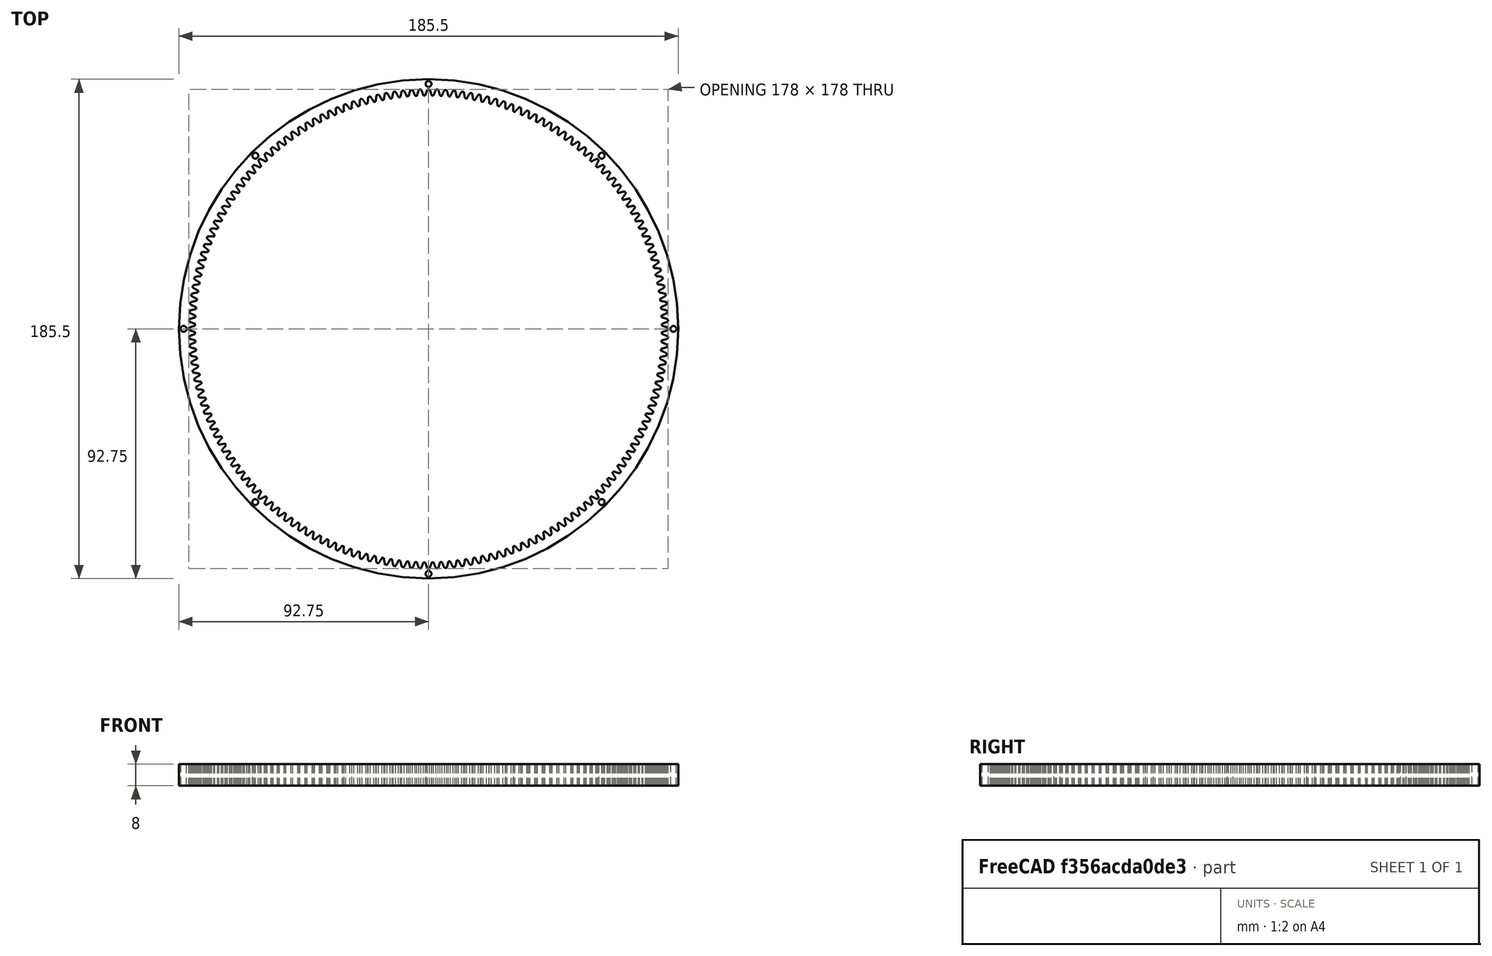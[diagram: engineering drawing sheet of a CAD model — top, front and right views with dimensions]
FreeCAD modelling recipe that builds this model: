
FCSTD DOCUMENT  (FreeCAD 0.19R24276 (Git))
Label: Out_gear_t176_d185_5_otv
License: All rights reserved
LicenseURL: http://en.wikipedia.org/wiki/All_rights_reserved
objects: Part::FeaturePython×1, Part::Cylinder×1, Part::Cut×1, Sketcher::SketchObject×1, PartDesign::FeatureBase×1, PartDesign::Pocket×1, PartDesign::Body×1
note: 8 computed .brp shape members not serialized (recipe doc carries the construction recipe); baked Part::Feature solids carry a one-line shape summary decoded from their .brp

FEATURE [Part::FeaturePython] involutegear  # WARN: FeaturePython — macro-defined, semantics opaque (R4)
  AttacherType = Attacher::AttachEngine3D
  backlash = 0
  beta = 0
  clearance = 0.25
  da = 178
  df = 173.5
  double_helix = false
  dw = 176
  head = 0
  height = 8
  module = 1
  numpoints = 6
  pressure_angle = 20
  properties_from_tool = false
  reversed_backlash = false
  shift = 0
  simple = false
  teeth = 176
  transverse_pitch = 3.14159
  undercut = false
  version = 0.0.3
FEATURE [Part::Cylinder] Cylinder  label="Цилиндр"
  Angle = 360
  AttacherType = Attacher::AttachEngine3D
  Height = 8
  Radius = 92.75
FEATURE [Part::Cut] Cut
  Base = -> Cylinder
  Tool = -> involutegear
FEATURE [Sketcher::SketchObject] Sketch
  FullyConstrained = false
  MapMode = 5
  Support = -> [XY_Plane]
  sketch-geometry (17):
    g0: LineSegment StartX=0 StartY=0 StartZ=0 EndX=64.3467 EndY=64.3467 EndZ=0
    g1: Circle CenterX=0 CenterY=0 CenterZ=0 NormalX=0 NormalY=0 NormalZ=1 AngleXU=0 Radius=91
    g2: Circle CenterX=64.3467 CenterY=64.3467 CenterZ=0 NormalX=0 NormalY=0 NormalZ=1 AngleXU=0 Radius=1.1
    g3: LineSegment StartX=0 StartY=0 StartZ=0 EndX=-1.5e-15 EndY=91 EndZ=0
    g4: LineSegment StartX=0 StartY=0 StartZ=0 EndX=91 EndY=0 EndZ=0
    g5: Circle CenterX=-1.5e-15 CenterY=91 CenterZ=0 NormalX=0 NormalY=0 NormalZ=1 AngleXU=0 Radius=1.1
    g6: Circle CenterX=91 CenterY=0 CenterZ=0 NormalX=0 NormalY=0 NormalZ=1 AngleXU=0 Radius=1.1
    g7: Circle CenterX=64.3467 CenterY=-64.3467 CenterZ=0 NormalX=0 NormalY=0 NormalZ=1 AngleXU=0 Radius=1.1
    g8: Circle CenterX=-1.5e-15 CenterY=-91 CenterZ=0 NormalX=0 NormalY=0 NormalZ=1 AngleXU=0 Radius=1.1
    g9: LineSegment StartX=0 StartY=0 StartZ=0 EndX=-1.5e-15 EndY=-91 EndZ=0
    g10: LineSegment StartX=0 StartY=0 StartZ=0 EndX=64.3467 EndY=-64.3467 EndZ=0
    g11: LineSegment StartX=0 StartY=0 StartZ=0 EndX=-64.3467 EndY=-64.3467 EndZ=0
    g12: LineSegment StartX=0 StartY=0 StartZ=0 EndX=-91 EndY=0 EndZ=0
    g13: LineSegment StartX=0 StartY=0 StartZ=0 EndX=-64.3467 EndY=64.3467 EndZ=0
    g14: Circle CenterX=-91 CenterY=0 CenterZ=0 NormalX=0 NormalY=0 NormalZ=1 AngleXU=0 Radius=1.1
    g15: Circle CenterX=-64.3467 CenterY=-64.3467 CenterZ=0 NormalX=0 NormalY=0 NormalZ=1 AngleXU=0 Radius=1.1
    g16: Circle CenterX=-64.3467 CenterY=64.3467 CenterZ=0 NormalX=0 NormalY=0 NormalZ=1 AngleXU=0 Radius=1.1
  constraints (26):
    c: Coincident(g0,g-1)
    c: Coincident(g1,g-1)
    c: Diameter(g1) = 182
    c: PointOnObject(g0,g1)
    c: Coincident(g2,g0)
    c: Diameter(g2) = 2.2
    c: Coincident(g3,g-1)
    c: Coincident(g4,g-1)
    c: PointOnObject(g4,g1)
    c: PointOnObject(g3,g1)
    c: Coincident(g5,g3)
    c: Coincident(g6,g4)
    c: Equal(g6,g2)
    c: Equal(g2,g5)
    c: Angle(g4,g-1) = 0
    c: Angle(g-1,g0) = 0.785398
    c: Angle(g0,g3) = 0.785398
    c: Coincident(g7,g10)
    c: Diameter(g7) = 2.2
    c: Coincident(g8,g9)
    c: Equal(g7,g8)
    c: Angle(g10,g9) = -0.785398
    c: Coincident(g14,g12)
    c: Coincident(g15,g11)
    c: Diameter(g15) = 2.2
    c: Diameter(g16) = 2.2
FEATURE [PartDesign::FeatureBase] BaseFeature
  BaseFeature = -> Cut
FEATURE [PartDesign::Pocket] Pocket
  BaseFeature = -> BaseFeature
  Length = 5
  Length2 = 100
  Profile = -> Sketch
  Reversed = true
  Type = 1
FEATURE [PartDesign::Body] Body
  BaseFeature = -> Cut
  Group = -> [BaseFeature,Sketch,Pocket]
  Origin = -> Origin
  Tip = -> Pocket
